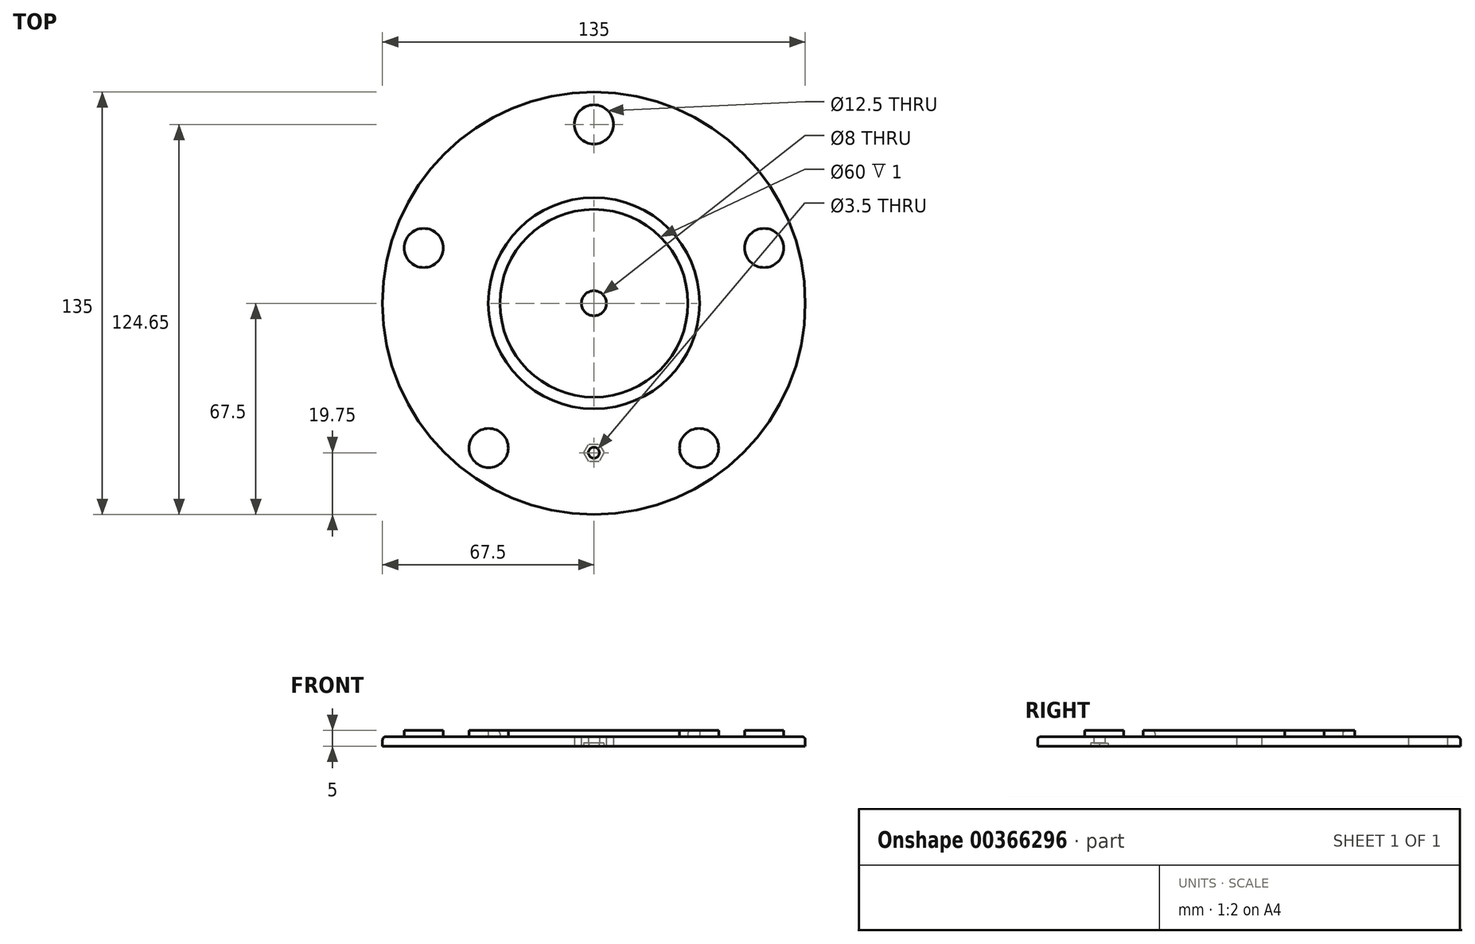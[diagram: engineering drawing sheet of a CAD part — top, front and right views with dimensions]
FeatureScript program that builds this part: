
annotation { "Feature Type Name" : "Feature", "Feature Type Description" : "" }
export const myFeature = defineFeature(function(context is Context, id is Id, definition is map)
    precondition{}
    {
        {
            var Q0;
            Q0=qCreatedBy(makeId("Top.planeOp"),FACE);
            var sketch = newSketch(context, id + "F0", { "sketchPlane" : qUnion([Q0])});
            skCircle(sketch, "E0", {"center": v(0, 0) * mm, "radius": 33.75 * mm});
            skCircle(sketch, "E1", {"center": v(0, 57.15) * mm, "radius": 6.25 * mm});
            skCircle(sketch, "E2.1.0", {"center": v(-54.35, 17.66) * mm, "radius": 6.25 * mm});
            skCircle(sketch, "E2.2.0", {"center": v(-33.6, -46.24) * mm, "radius": 6.25 * mm});
            skCircle(sketch, "E2.3.0", {"center": v(33.6, -46.24) * mm, "radius": 6.25 * mm});
            skCircle(sketch, "E2.4.0", {"center": v(54.35, 17.66) * mm, "radius": 6.25 * mm});
            skCircle(sketch, "E3", {"center": v(0, 0) * mm, "radius": 57.15 * mm});
            skCircle(sketch, "E4", {"center": v(0, 0) * mm, "radius": 4 * mm});
            skCircle(sketch, "E5", {"center": v(0, 0) * mm, "radius": 67.5 * mm});
            skCircle(sketch, "E6", {"center": v(0, 0) * mm, "radius": 30 * mm});
            skCircle(sketch, "E7", {"center": v(0, -47.75) * mm, "radius": 1.75 * mm});
            skCircle(sketch, "E8.cCircle", {"center": v(0, -47.75) * mm, "radius": 2.8 * mm, "construction": true});
            skLineSegment(sketch, "E8.0", {"start": v(1.62, -50.55) * mm, "end": v(-1.62, -50.55) * mm});
            skLineSegment(sketch, "E8.1", {"start": v(-1.62, -50.55) * mm, "end": v(-3.23, -47.75) * mm});
            skLineSegment(sketch, "E8.2", {"start": v(-3.23, -47.75) * mm, "end": v(-1.62, -44.95) * mm});
            skLineSegment(sketch, "E8.3", {"start": v(-1.62, -44.95) * mm, "end": v(1.62, -44.95) * mm});
            skLineSegment(sketch, "E8.4", {"start": v(1.62, -44.95) * mm, "end": v(3.23, -47.75) * mm});
            skLineSegment(sketch, "E8.5", {"start": v(3.23, -47.75) * mm, "end": v(1.62, -50.55) * mm});
            skPoint(sketch, "E8.0.midPoint", {"position": v(0, -50.55) * mm});
            skSolve(sketch);
        }
        {
            var Q0;
            Q0=makeQuery(id+"F0.imprint","IMPRINT",FACE,{"disambiguationData":[TD([[makeQuery(id+"F0.imprint","IMPRINT",EDGE,{"derivedFrom":sQuery(id+"F0.wireOp",EDGE,"E0")}),-1.0]])]});
            var Q1;
            Q1=makeQuery(id+"F0.imprint","IMPRINT",FACE,{"disambiguationData":[TD([[makeQuery(id+"F0.imprint","IMPRINT",EDGE,{"derivedFrom":sQuery(id+"F0.wireOp",EDGE,"E5")}),1.0]])]});
            var Q2;
            Q2=makeQuery(id+"F0.imprint","IMPRINT",FACE,{"disambiguationData":[TD([[makeQuery(id+"F0.imprint","IMPRINT",EDGE,{"derivedFrom":sQuery(id+"F0.wireOp",EDGE,"E4")}),-1.0]])]});
            extrude(context, id + "F1", {"entities" : qUnion([Q0, Q1, Q2]), "depth" : 3 * mm});
        }
        {
            var Q0;
            Q0=makeQuery(id+"F0.imprint","IMPRINT",FACE,{"disambiguationData":[TD([[makeQuery(id+"F0.imprint","IMPRINT",EDGE,{"derivedFrom":sQuery(id+"F0.wireOp",EDGE,"E0")}),1.0]])]});
            var Q1;
            {var subQ0=sQuery(id+"F0.wireOp",EDGE,"E3");var subQ1=sQuery(id+"F0.wireOp",EDGE,"E2.1.0");var subQ2=makeQuery(id+"F0.imprint","INTERSECT",VERTEX,{"disambiguationData":[OD(0.0)],"derivedFrom":[subQ1,subQ0]});Q1=makeQuery(id+"F0.imprint","IMPRINT",FACE,{"disambiguationData":[TD([[makeQuery(id+"F0.imprint","IMPRINT",EDGE,{"disambiguationData":[TD([[subQ2,1.0]])],"derivedFrom":subQ1}),1.0]])]});}
            var Q2;
            {var subQ0=sQuery(id+"F0.wireOp",EDGE,"E3");var subQ1=sQuery(id+"F0.wireOp",EDGE,"E2.1.0");var subQ2=makeQuery(id+"F0.imprint","INTERSECT",VERTEX,{"disambiguationData":[OD(0.0)],"derivedFrom":[subQ1,subQ0]});Q2=makeQuery(id+"F0.imprint","IMPRINT",FACE,{"disambiguationData":[TD([[makeQuery(id+"F0.imprint","IMPRINT",EDGE,{"disambiguationData":[TD([[subQ2,-1.0]])],"derivedFrom":subQ1}),1.0]])]});}
            var Q3;
            {var subQ0=sQuery(id+"F0.wireOp",EDGE,"E3");var subQ1=sQuery(id+"F0.wireOp",EDGE,"E2.4.0");var subQ2=makeQuery(id+"F0.imprint","INTERSECT",VERTEX,{"disambiguationData":[OD(0.0)],"derivedFrom":[subQ1,subQ0]});Q3=makeQuery(id+"F0.imprint","IMPRINT",FACE,{"disambiguationData":[TD([[makeQuery(id+"F0.imprint","IMPRINT",EDGE,{"disambiguationData":[TD([[subQ2,1.0]])],"derivedFrom":subQ1}),1.0]])]});}
            var Q4;
            {var subQ0=sQuery(id+"F0.wireOp",EDGE,"E3");var subQ1=sQuery(id+"F0.wireOp",EDGE,"E2.4.0");var subQ2=makeQuery(id+"F0.imprint","INTERSECT",VERTEX,{"disambiguationData":[OD(0.0)],"derivedFrom":[subQ1,subQ0]});Q4=makeQuery(id+"F0.imprint","IMPRINT",FACE,{"disambiguationData":[TD([[makeQuery(id+"F0.imprint","IMPRINT",EDGE,{"disambiguationData":[TD([[subQ2,-1.0]])],"derivedFrom":subQ1}),1.0]])]});}
            var Q5;
            {var subQ0=sQuery(id+"F0.wireOp",EDGE,"E3");var subQ1=sQuery(id+"F0.wireOp",EDGE,"E2.3.0");var subQ2=makeQuery(id+"F0.imprint","INTERSECT",VERTEX,{"disambiguationData":[OD(0.0)],"derivedFrom":[subQ1,subQ0]});Q5=makeQuery(id+"F0.imprint","IMPRINT",FACE,{"disambiguationData":[TD([[makeQuery(id+"F0.imprint","IMPRINT",EDGE,{"disambiguationData":[TD([[subQ2,-1.0]])],"derivedFrom":subQ1}),1.0]])]});}
            var Q6;
            {var subQ0=sQuery(id+"F0.wireOp",EDGE,"E3");var subQ1=sQuery(id+"F0.wireOp",EDGE,"E2.3.0");var subQ2=makeQuery(id+"F0.imprint","INTERSECT",VERTEX,{"disambiguationData":[OD(0.0)],"derivedFrom":[subQ1,subQ0]});Q6=makeQuery(id+"F0.imprint","IMPRINT",FACE,{"disambiguationData":[TD([[makeQuery(id+"F0.imprint","IMPRINT",EDGE,{"disambiguationData":[TD([[subQ2,1.0]])],"derivedFrom":subQ1}),1.0]])]});}
            var Q7;
            {var subQ0=sQuery(id+"F0.wireOp",EDGE,"E3");var subQ1=sQuery(id+"F0.wireOp",EDGE,"E2.2.0");var subQ2=makeQuery(id+"F0.imprint","INTERSECT",VERTEX,{"disambiguationData":[OD(0.0)],"derivedFrom":[subQ1,subQ0]});Q7=makeQuery(id+"F0.imprint","IMPRINT",FACE,{"disambiguationData":[TD([[makeQuery(id+"F0.imprint","IMPRINT",EDGE,{"disambiguationData":[TD([[subQ2,1.0]])],"derivedFrom":subQ1}),1.0]])]});}
            var Q8;
            {var subQ0=sQuery(id+"F0.wireOp",EDGE,"E3");var subQ1=sQuery(id+"F0.wireOp",EDGE,"E2.2.0");var subQ2=makeQuery(id+"F0.imprint","INTERSECT",VERTEX,{"disambiguationData":[OD(0.0)],"derivedFrom":[subQ1,subQ0]});Q8=makeQuery(id+"F0.imprint","IMPRINT",FACE,{"disambiguationData":[TD([[makeQuery(id+"F0.imprint","IMPRINT",EDGE,{"disambiguationData":[TD([[subQ2,-1.0]])],"derivedFrom":subQ1}),1.0]])]});}
            extrude(context, id + "F2", {"entities" : qUnion([Q0, Q1, Q2, Q3, Q4, Q5, Q6, Q7, Q8]), "operationType" : NewBodyOperationType.ADD, "depth" : 5 * mm});
        }
        {
            var Q0;
            {var subQ0=sQuery(id+"F0.wireOp",EDGE,"E8.3");Q0=makeQuery(id+"F0.imprint","IMPRINT",FACE,{"disambiguationData":[TD([[makeQuery(id+"F0.imprint","IMPRINT",EDGE,{"derivedFrom":subQ0}),-1.0]])]});}
            var Q1;
            Q1=makeQuery(id+"F0.imprint","IMPRINT",FACE,{"disambiguationData":[TD([[makeQuery(id+"F0.imprint","IMPRINT",EDGE,{"derivedFrom":sQuery(id+"F0.wireOp",EDGE,"E8.0")}),-1.0]])]});
            extrude(context, id + "F3", {"entities" : qUnion([Q0, Q1]), "operationType" : NewBodyOperationType.ADD, "depth" : 3 * mm, "hasSecondDirection" : true, "secondDirectionOppositeDirection" : false, "secondDirectionDepth" : 1 * mm});
        }
        {
            var Q0;
            Q0=makeQuery(id+"F1.opExtrude","CAP_EDGE",EDGE,{"disambiguationData":[OSD([sQuery(id+"F0.wireOp",EDGE,"E5")])],"isStart":false});
            var Q1;
            Q1=makeQuery(id+"F2.opExtrude","CAP_EDGE",EDGE,{"disambiguationData":[OSD([sQuery(id+"F0.wireOp",EDGE,"E6")])],"isStart":false});
            fillet(context, id + "F4", {"entities" : qUnion([Q0, Q1]), "radius" : 1 * mm, "tangentPropagation" : true, "allowEdgeOverflow" : false});
        }
    });
